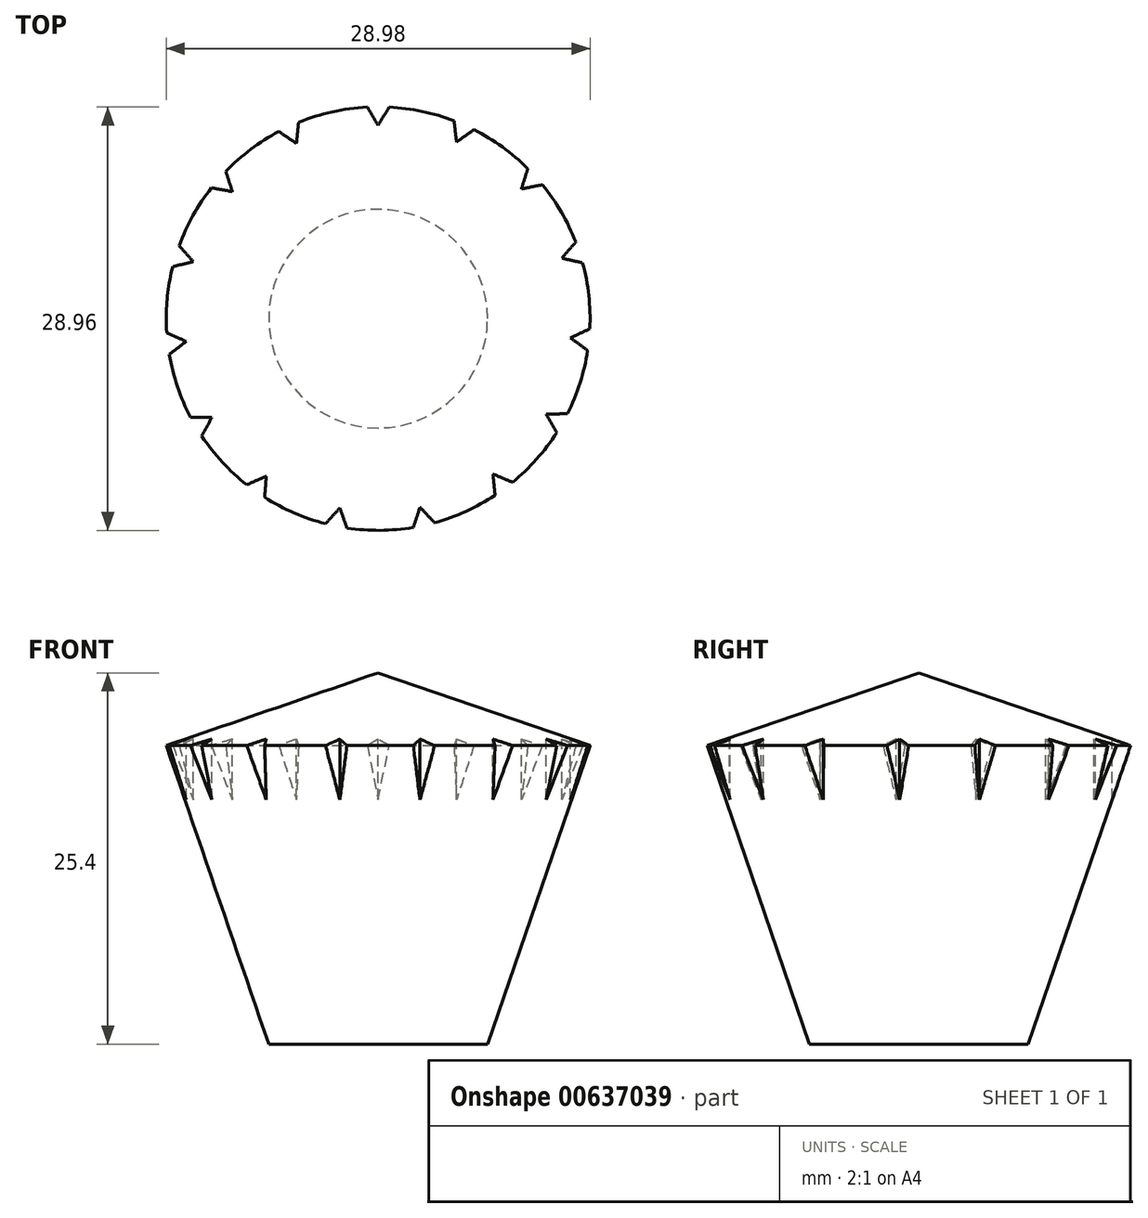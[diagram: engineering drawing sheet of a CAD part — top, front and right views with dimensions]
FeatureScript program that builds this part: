
annotation { "Feature Type Name" : "Feature", "Feature Type Description" : "" }
export const myFeature = defineFeature(function(context is Context, id is Id, definition is map)
    precondition{}
    {
        {
            var Q0;
            Q0=qCreatedBy(makeId("Front.planeOp"),FACE);
            var sketch = newSketch(context, id + "F0", { "sketchPlane" : qUnion([Q0])});
            skLineSegment(sketch, "E0", {"start": v(0, 0) * mm, "end": v(0, 25.4) * mm});
            skLineSegment(sketch, "E1", {"start": v(0, 25.4) * mm, "end": v(-14.5, 20.43) * mm});
            skLineSegment(sketch, "E2", {"start": v(-14.5, 20.43) * mm, "end": v(-7.48, 0) * mm});
            skLineSegment(sketch, "E3", {"start": v(-7.48, 0) * mm, "end": v(0, 0) * mm});
            skLineSegment(sketch, "E4.bottom", {"start": v(-3.17, 0) * mm, "end": v(0, 0) * mm});
            skLineSegment(sketch, "E4.top", {"start": v(-3.17, -12.7) * mm, "end": v(0, -12.7) * mm});
            skLineSegment(sketch, "E4.left", {"start": v(-3.18, 0) * mm, "end": v(-3.17, -12.7) * mm});
            skLineSegment(sketch, "E4.right", {"start": v(0, 0) * mm, "end": v(0, -12.7) * mm});
            skSolve(sketch);
        }
        {
            var Q0;
            Q0=makeQuery(id+"F0.imprint","IMPRINT",FACE,{"disambiguationData":[TD([[makeQuery(id+"F0.imprint","IMPRINT",EDGE,{"derivedFrom":sQuery(id+"F0.wireOp",EDGE,"E0")}),1.0]])]});
            var Q1;
            Q1=makeQuery(id+"F0.imprint","IMPRINT",FACE,{"disambiguationData":[TD([[makeQuery(id+"F0.imprint","IMPRINT",EDGE,{"derivedFrom":sQuery(id+"F0.wireOp",EDGE,"E4.bottom")}),-1.0]])]});
            var Q2;
            Q2=sQuery(id+"F0.wireOp",EDGE,"E0");
            revolve(context, id + "F1", {"entities" : qUnion([Q0, Q1]), "axis" : qUnion([Q2]), "revolveType" : RevolveType.FULL});
        }
        {
            var Q0;
            Q0=qCreatedBy(makeId("Top.planeOp"),FACE);
            cPlane(context, id + "F2", {"entities" : qUnion([Q0]), "cplaneType" : CPlaneType.OFFSET, "offset" : 25.4 * mm, "width" : 152.4 * mm, "height" : 152.4 * mm});
        }
        {
            var Q0;
            Q0=qCreatedBy(id+"F2.planeOp",FACE);
            var sketch = newSketch(context, id + "F3", { "sketchPlane" : qUnion([Q0])});
            skLineSegment(sketch, "E5", {"start": v(0, 13.22) * mm, "end": v(2.32, 17.12) * mm});
            skLineSegment(sketch, "E6", {"start": v(2.32, 17.12) * mm, "end": v(0, 13.22) * mm});
            skLineSegment(sketch, "E7", {"start": v(-2.32, 17.12) * mm, "end": v(0, 13.22) * mm});
            skLineSegment(sketch, "E8", {"start": v(2.32, 17.12) * mm, "end": v(-2.32, 17.12) * mm});
            skLineSegment(sketch, "E9.1.0", {"start": v(9.07, 14.7) * mm, "end": v(5.36, 12.08) * mm});
            skLineSegment(sketch, "E9.1.1", {"start": v(4.82, 16.6) * mm, "end": v(5.36, 12.08) * mm});
            skLineSegment(sketch, "E9.1.2", {"start": v(9.07, 14.7) * mm, "end": v(4.82, 16.6) * mm});
            skLineSegment(sketch, "E9.2.0", {"start": v(14.25, 9.77) * mm, "end": v(9.8, 8.87) * mm});
            skLineSegment(sketch, "E9.2.1", {"start": v(11.14, 13.21) * mm, "end": v(9.8, 8.87) * mm});
            skLineSegment(sketch, "E9.2.2", {"start": v(14.25, 9.77) * mm, "end": v(11.14, 13.21) * mm});
            skLineSegment(sketch, "E9.3.0", {"start": v(16.99, 3.15) * mm, "end": v(12.56, 4.13) * mm});
            skLineSegment(sketch, "E9.3.1", {"start": v(15.54, 7.56) * mm, "end": v(12.56, 4.13) * mm});
            skLineSegment(sketch, "E9.3.2", {"start": v(16.99, 3.15) * mm, "end": v(15.54, 7.56) * mm});
            skLineSegment(sketch, "E9.4.0", {"start": v(16.8, -4.02) * mm, "end": v(13.15, -1.32) * mm});
            skLineSegment(sketch, "E9.4.1", {"start": v(17.27, 0.6) * mm, "end": v(13.15, -1.32) * mm});
            skLineSegment(sketch, "E9.4.2", {"start": v(16.8, -4.02) * mm, "end": v(17.27, 0.6) * mm});
            skLineSegment(sketch, "E9.5.0", {"start": v(13.73, -10.49) * mm, "end": v(11.49, -6.54) * mm});
            skLineSegment(sketch, "E9.5.1", {"start": v(16.03, -6.45) * mm, "end": v(11.49, -6.54) * mm});
            skLineSegment(sketch, "E9.5.2", {"start": v(13.73, -10.49) * mm, "end": v(16.03, -6.45) * mm});
            skLineSegment(sketch, "E9.6.0", {"start": v(8.3, -15.16) * mm, "end": v(7.85, -10.64) * mm});
            skLineSegment(sketch, "E9.6.1", {"start": v(12.04, -12.4) * mm, "end": v(7.85, -10.64) * mm});
            skLineSegment(sketch, "E9.6.2", {"start": v(8.3, -15.16) * mm, "end": v(12.04, -12.4) * mm});
            skLineSegment(sketch, "E9.7.0", {"start": v(1.44, -17.22) * mm, "end": v(2.86, -12.9) * mm});
            skLineSegment(sketch, "E9.7.1", {"start": v(5.97, -16.21) * mm, "end": v(2.86, -12.9) * mm});
            skLineSegment(sketch, "E9.7.2", {"start": v(1.44, -17.22) * mm, "end": v(5.97, -16.21) * mm});
            skLineSegment(sketch, "E9.8.0", {"start": v(-5.67, -16.32) * mm, "end": v(-2.62, -12.96) * mm});
            skLineSegment(sketch, "E9.8.1", {"start": v(-1.12, -17.24) * mm, "end": v(-2.62, -12.96) * mm});
            skLineSegment(sketch, "E9.8.2", {"start": v(-5.67, -16.32) * mm, "end": v(-1.12, -17.24) * mm});
            skLineSegment(sketch, "E9.9.0", {"start": v(-11.8, -12.62) * mm, "end": v(-7.65, -10.78) * mm});
            skLineSegment(sketch, "E9.9.1", {"start": v(-8.01, -15.3) * mm, "end": v(-7.65, -10.78) * mm});
            skLineSegment(sketch, "E9.9.2", {"start": v(-11.8, -12.62) * mm, "end": v(-8.01, -15.3) * mm});
            skLineSegment(sketch, "E9.10.0", {"start": v(-15.9, -6.75) * mm, "end": v(-11.36, -6.75) * mm});
            skLineSegment(sketch, "E9.10.1", {"start": v(-13.53, -10.74) * mm, "end": v(-11.36, -6.75) * mm});
            skLineSegment(sketch, "E9.10.2", {"start": v(-15.9, -6.75) * mm, "end": v(-13.53, -10.74) * mm});
            skLineSegment(sketch, "E9.11.0", {"start": v(-17.28, 0.28) * mm, "end": v(-13.13, -1.56) * mm});
            skLineSegment(sketch, "E9.11.1", {"start": v(-16.73, -4.33) * mm, "end": v(-13.13, -1.56) * mm});
            skLineSegment(sketch, "E9.11.2", {"start": v(-17.28, 0.28) * mm, "end": v(-16.73, -4.33) * mm});
            skLineSegment(sketch, "E9.12.0", {"start": v(-15.68, 7.27) * mm, "end": v(-12.63, 3.9) * mm});
            skLineSegment(sketch, "E9.12.1", {"start": v(-17.05, 2.83) * mm, "end": v(-12.63, 3.9) * mm});
            skLineSegment(sketch, "E9.12.2", {"start": v(-15.68, 7.27) * mm, "end": v(-17.05, 2.83) * mm});
            skLineSegment(sketch, "E9.13.0", {"start": v(-11.38, 13) * mm, "end": v(-9.96, 8.68) * mm});
            skLineSegment(sketch, "E9.13.1", {"start": v(-14.43, 9.5) * mm, "end": v(-9.96, 8.68) * mm});
            skLineSegment(sketch, "E9.13.2", {"start": v(-11.38, 13) * mm, "end": v(-14.43, 9.5) * mm});
            skLineSegment(sketch, "E9.14.0", {"start": v(-5.13, 16.5) * mm, "end": v(-5.59, 11.98) * mm});
            skLineSegment(sketch, "E9.14.1", {"start": v(-9.34, 14.54) * mm, "end": v(-5.59, 11.98) * mm});
            skLineSegment(sketch, "E9.14.2", {"start": v(-5.13, 16.5) * mm, "end": v(-9.34, 14.54) * mm});
            skPoint(sketch, "E9.center", {"position": v(0, 0) * mm});
            skLineSegment(sketch, "E9.anchor1", {"start": v(0, 0) * mm, "end": v(0, 13.22) * mm, "construction": true});
            skLineSegment(sketch, "E9.anchor2", {"start": v(0, 0) * mm, "end": v(-5.59, 11.98) * mm, "construction": true});
            skSolve(sketch);
        }
        {
            var Q0;
            Q0 = qSketchRegion(id + "F3", true);
            extrude(context, id + "F4", {"entities" : qUnion([Q0]), "operationType" : NewBodyOperationType.REMOVE, "oppositeDirection" : true, "depth" : 25.4 * mm, "offsetDistance" : 25.4 * mm});
        }
    });
